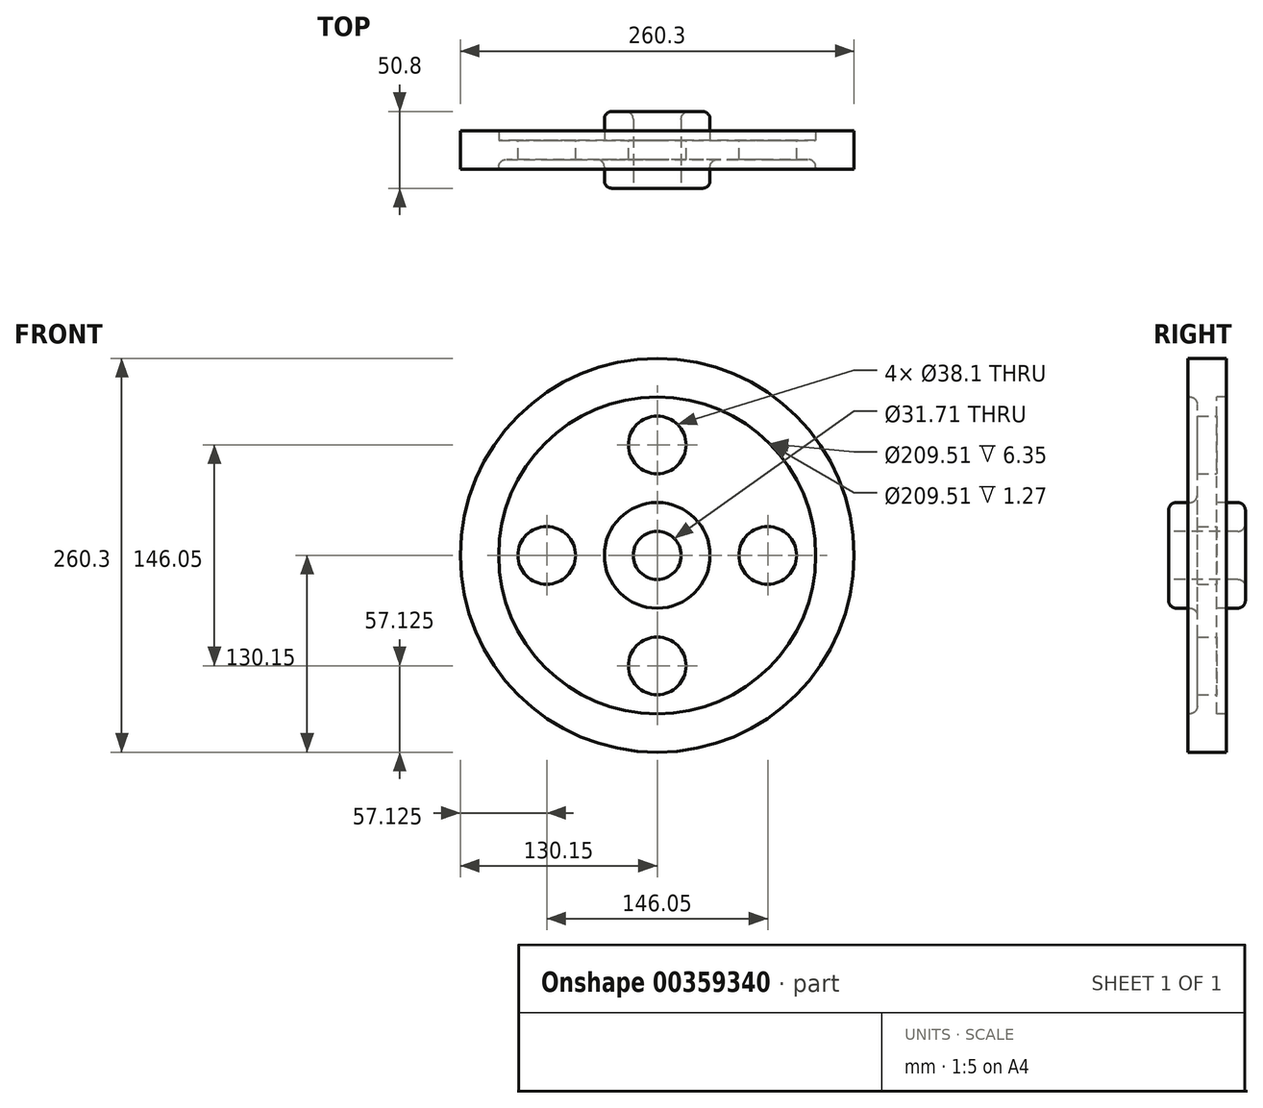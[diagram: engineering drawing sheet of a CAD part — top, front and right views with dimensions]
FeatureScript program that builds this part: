
annotation { "Feature Type Name" : "Feature", "Feature Type Description" : "" }
export const myFeature = defineFeature(function(context is Context, id is Id, definition is map)
    precondition{}
    {
        {
            var Q0;
            Q0=qCreatedBy(makeId("Right.planeOp"),FACE);
            var sketch = newSketch(context, id + "F0", { "sketchPlane" : qUnion([Q0])});
            skLineSegment(sketch, "E0", {"start": v(0, -3.2) * mm, "end": v(0, 25.38) * mm});
            skLineSegment(sketch, "E1", {"start": v(0, 25.38) * mm, "end": v(0, 69.83) * mm});
            skLineSegment(sketch, "E2", {"start": v(0, 69.83) * mm, "end": v(0, 117.45) * mm});
            skLineSegment(sketch, "E3.bottom", {"start": v(-25.4, 15.85) * mm, "end": v(25.4, 15.85) * mm});
            skLineSegment(sketch, "E3.top", {"start": v(-25.4, 34.9) * mm, "end": v(-6.35, 34.9) * mm});
            skLineSegment(sketch, "E3.left", {"start": v(-25.4, 15.85) * mm, "end": v(-25.4, 34.9) * mm});
            skLineSegment(sketch, "E3.right", {"start": v(25.4, 15.85) * mm, "end": v(25.4, 34.9) * mm});
            skPoint(sketch, "E3.middle", {"position": v(0, 25.38) * mm});
            skLineSegment(sketch, "E4.bottom", {"start": v(12.7, 130.15) * mm, "end": v(-12.7, 130.15) * mm});
            skLineSegment(sketch, "E4.top", {"start": v(12.7, 104.75) * mm, "end": v(6.35, 104.75) * mm});
            skLineSegment(sketch, "E4.left", {"start": v(12.7, 130.15) * mm, "end": v(12.7, 104.75) * mm});
            skLineSegment(sketch, "E4.right", {"start": v(-12.7, 130.15) * mm, "end": v(-12.7, 104.75) * mm});
            skPoint(sketch, "E4.middle", {"position": v(0, 117.45) * mm});
            skLineSegment(sketch, "E5.left", {"start": v(6.35, 31.73) * mm, "end": v(6.35, 107.93) * mm});
            skLineSegment(sketch, "E5.right", {"start": v(-6.35, 31.73) * mm, "end": v(-6.35, 107.93) * mm});
            skPoint(sketch, "E5.middle", {"position": v(0, 69.83) * mm});
            skLineSegment(sketch, "E6.trimOffspring", {"start": v(-6.35, 104.75) * mm, "end": v(-12.7, 104.75) * mm});
            skLineSegment(sketch, "E7.trimOffspring", {"start": v(6.35, 34.9) * mm, "end": v(25.4, 34.9) * mm});
            skLineSegment(sketch, "E8", {"start": v(0, 0) * mm, "end": v(23.06, 0) * mm});
            skSolve(sketch);
        }
        {
            var Q0;
            {var subQ1=sQuery(id+"F0.wireOp",EDGE,"E3.top");Q0=makeQuery(id+"F0.imprint","IMPRINT",FACE,{"disambiguationData":[TD([[makeQuery(id+"F0.imprint","IMPRINT",EDGE,{"derivedFrom":subQ1}),-1.0]])]});}
            var Q1;
            Q1=sQuery(id+"F0.wireOp",EDGE,"E8");
            revolve(context, id + "F1", {"entities" : qUnion([Q0]), "axis" : qUnion([Q1]), "revolveType" : RevolveType.FULL});
        }
        {
            var Q0;
            Q0=makeQuery(id+"F1.opRevolve","SWEPT_FACE",FACE,{"disambiguationData":[OSD([sQuery(id+"F0.wireOp",EDGE,"E5.left")])]});
            var sketch = newSketch(context, id + "F2", { "sketchPlane" : qUnion([Q0])});
            skLineSegment(sketch, "E9", {"start": v(0, 0) * mm, "end": v(0, 73.03) * mm});
            skCircle(sketch, "E10", {"center": v(0, 73.03) * mm, "radius": 19.05 * mm});
            skCircle(sketch, "E11.1.0", {"center": v(-73.03, 0) * mm, "radius": 19.05 * mm});
            skCircle(sketch, "E11.2.0", {"center": v(0, -73.03) * mm, "radius": 19.05 * mm});
            skCircle(sketch, "E11.3.0", {"center": v(73.03, 0) * mm, "radius": 19.05 * mm});
            skPoint(sketch, "E11.center", {"position": v(0, 0) * mm});
            skSolve(sketch);
        }
        {
            var Q0;
            Q0=makeQuery(id+"F2.imprint","IMPRINT",FACE,{"disambiguationData":[TD([[makeQuery(id+"F2.imprint","IMPRINT",EDGE,{"derivedFrom":sQuery(id+"F2.wireOp",EDGE,"E10")}),1.0]])]});
            var Q1;
            Q1=makeQuery(id+"F2.imprint","IMPRINT",FACE,{"disambiguationData":[TD([[makeQuery(id+"F2.imprint","IMPRINT",EDGE,{"derivedFrom":sQuery(id+"F2.wireOp",EDGE,"E11.3.0")}),1.0]])]});
            var Q2;
            Q2=makeQuery(id+"F2.imprint","IMPRINT",FACE,{"disambiguationData":[TD([[makeQuery(id+"F2.imprint","IMPRINT",EDGE,{"derivedFrom":sQuery(id+"F2.wireOp",EDGE,"E11.2.0")}),1.0]])]});
            var Q3;
            Q3=makeQuery(id+"F2.imprint","IMPRINT",FACE,{"disambiguationData":[TD([[makeQuery(id+"F2.imprint","IMPRINT",EDGE,{"derivedFrom":sQuery(id+"F2.wireOp",EDGE,"E11.1.0")}),1.0]])]});
            extrude(context, id + "F3", {"entities" : qUnion([Q0, Q1, Q2, Q3]), "operationType" : NewBodyOperationType.REMOVE, "oppositeDirection" : true, "depth" : 25.4 * mm});
        }
        {
            var Q0;
            Q0=makeQuery(id+"F1.opRevolve","SWEPT_EDGE",EDGE,{"disambiguationData":[OSD([sQuery(id+"F0.wireOp",EDGE,"E3.top"),sQuery(id+"F0.wireOp",EDGE,"E3.left")])]});
            var Q1;
            Q1=makeQuery(id+"F1.opRevolve","SWEPT_FACE",FACE,{"disambiguationData":[OSD([sQuery(id+"F0.wireOp",EDGE,"E3.top")])]});
            fillet(context, id + "F4", {"entities" : qUnion([Q0, Q1]), "radius" : 5.08 * mm, "tangentPropagation" : true, "allowEdgeOverflow" : false});
        }
        {
            var Q0;
            Q0=makeQuery(id+"F1.opRevolve","SWEPT_EDGE",EDGE,{"disambiguationData":[OSD([sQuery(id+"F0.wireOp",EDGE,"E5.right"),sQuery(id+"F0.wireOp",EDGE,"E6.trimOffspring")])]});
            fillet(context, id + "F5", {"entities" : qUnion([Q0]), "radius" : 5.08 * mm, "tangentPropagation" : true, "allowEdgeOverflow" : false});
        }
        {
            var Q0;
            Q0=makeQuery(id+"F1.opRevolve","SWEPT_FACE",FACE,{"disambiguationData":[OSD([sQuery(id+"F0.wireOp",EDGE,"E3.right")])]});
            fillet(context, id + "F6", {"entities" : qUnion([Q0]), "radius" : 5.08 * mm, "tangentPropagation" : true, "allowEdgeOverflow" : false});
        }
    });
